# Revit family: Furniture-Table-Midmark-Ritter-225-Power_Examination1
name_source: partatom
category: Furniture
revit_build: Autodesk Revit 2016 (Build: 20170117_1200(x64)
units: mm (PartAtom-declared; Revit-internal decimal feet)

## family parameters
Always vertical = Yes
Cut with Voids When Loaded = No
OmniClass Number = 23.40.70.11.14.11.14
OmniClass Title = Examination and Treatment Equipment
Room Calculation Point = No
Shared = No
Work Plane-Based = No

## types (2) — shared parameters
Amps = 12 A
Apparent Load = 1323 VA
Assembly Code = E1020810
Connector Description = Power Connector
Description = Ritter 225 Barrier-Free Power Examination Table
Manufacturer = Midmark
Model = Ritter 225
Number of Poles = 1
Patient Weight Capacity = 500.00 lb
Power Factor = 1
Product Documentation Link = http://www.midmark.com
Product Page URL = http://www.midmark.com
URL = http://www.midmark.com
Voltage = 115 V
Weight = 409.00 lb

## type names (no varying parameters)
- 225-002
- 225-003

## geometry (parser evidence)
native form markers: Blend x8, Sweep x33
no freeform markers — native parametric forms only
